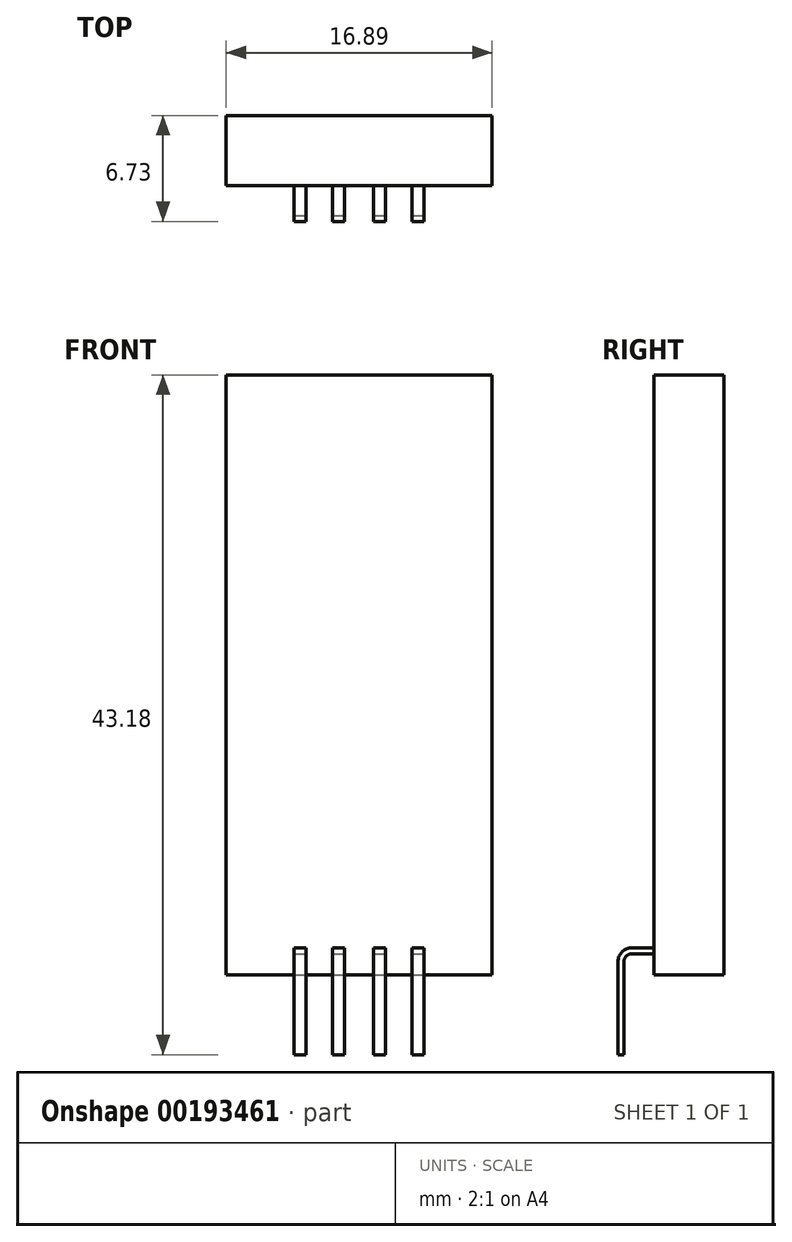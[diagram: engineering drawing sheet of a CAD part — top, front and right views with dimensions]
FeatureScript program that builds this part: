
annotation { "Feature Type Name" : "Feature", "Feature Type Description" : "" }
export const myFeature = defineFeature(function(context is Context, id is Id, definition is map)
    precondition{}
    {
        {
            var Q0;
            Q0=qCreatedBy(makeId("Front.planeOp"),FACE);
            var sketch = newSketch(context, id + "F0", { "sketchPlane" : qUnion([Q0])});
            skLineSegment(sketch, "E0.bottom", {"start": v(0, 0) * mm, "end": v(16.9, 0) * mm});
            skLineSegment(sketch, "E0.top", {"start": v(0, 38.1) * mm, "end": v(16.9, 38.1) * mm});
            skLineSegment(sketch, "E0.left", {"start": v(0, 0) * mm, "end": v(0, 38.1) * mm});
            skLineSegment(sketch, "E0.right", {"start": v(16.9, 0) * mm, "end": v(16.9, 38.1) * mm});
            skSolve(sketch);
        }
        {
            var Q0;
            Q0=makeQuery(id+"F0.imprint","IMPRINT",FACE,{"disambiguationData":[TD([[makeQuery(id+"F0.imprint","IMPRINT",EDGE,{"derivedFrom":sQuery(id+"F0.wireOp",EDGE,"E0.bottom")}),1.0]])]});
            extrude(context, id + "F1", {"entities" : qUnion([Q0]), "depth" : 4.44 * mm});
        }
        {
            var Q0;
            Q0=makeQuery(id+"F1.opExtrude","SWEPT_FACE",FACE,{"disambiguationData":[OSD([sQuery(id+"F0.wireOp",EDGE,"E0.right")])]});
            var sketch = newSketch(context, id + "F2", { "sketchPlane" : qUnion([Q0])});
            skLineSegment(sketch, "E1", {"start": v(-6.35, -5.08) * mm, "end": v(-6.35, 0.82) * mm});
            skLineSegment(sketch, "E2", {"start": v(-5.84, 1.33) * mm, "end": v(-4.45, 1.33) * mm});
            skArc(sketch, "E3.filletArc", {"start": v(-5.84, 1.33) * mm, "mid": v(-6.2, 1.18) * mm, "end": v(-6.35, 0.82) * mm});
            skLineSegment(sketch, "E4.0", {"start": v(-5.84, 1.71) * mm, "end": v(-4.45, 1.71) * mm});
            skArc(sketch, "E4.1", {"start": v(-5.84, 1.71) * mm, "mid": v(-6.47, 1.45) * mm, "end": v(-6.73, 0.82) * mm});
            skLineSegment(sketch, "E4.2", {"start": v(-6.73, -5.08) * mm, "end": v(-6.73, 0.82) * mm});
            skLineSegment(sketch, "E5", {"start": v(-6.73, -5.08) * mm, "end": v(-6.35, -5.08) * mm});
            skLineSegment(sketch, "E6", {"start": v(-4.45, 1.33) * mm, "end": v(-4.45, 1.71) * mm});
            skSolve(sketch);
        }
        {
            var Q0;
            Q0=makeQuery(id+"F2.imprint","IMPRINT",FACE,{"disambiguationData":[TD([[makeQuery(id+"F2.imprint","IMPRINT",EDGE,{"derivedFrom":sQuery(id+"F2.wireOp",EDGE,"E1")}),1.0]])]});
            var Q1;
            Q1=makeQuery(id+"F1.opExtrude","SWEPT_FACE",FACE,{"disambiguationData":[OSD([sQuery(id+"F0.wireOp",EDGE,"E0.left")])]});
            extrude(context, id + "F3", {"entities" : qUnion([Q0]), "endBound" : BoundingType.UP_TO_SURFACE, "oppositeDirection" : true, "endBoundEntityFace" : qUnion([Q1]), "depth" : 25.4 * mm});
        }
        {
            var Q0;
            Q0=makeQuery(id+"F1.opExtrude","CAP_FACE",FACE,{"disambiguationData":[OSD([sQuery(id+"F0.wireOp",EDGE,"E0.bottom"),sQuery(id+"F0.wireOp",EDGE,"E0.top"),sQuery(id+"F0.wireOp",EDGE,"E0.left"),sQuery(id+"F0.wireOp",EDGE,"E0.right")])],"isStart":false});
            var sketch = newSketch(context, id + "F4", { "sketchPlane" : qUnion([Q0])});
            skLineSegment(sketch, "E7", {"start": v(8.45, -5.17) * mm, "end": v(8.45, 2.43) * mm, "construction": true});
            skPoint(sketch, "E7.startSnap0", {"position": v(8.45, 38.1) * mm});
            skPoint(sketch, "E7.endSnap0", {"position": v(8.45, 0) * mm});
            skLineSegment(sketch, "E8", {"start": v(4.32, -6.24) * mm, "end": v(4.32, 3.07) * mm});
            skLineSegment(sketch, "E9", {"start": v(5.08, -6.3) * mm, "end": v(5.08, 3) * mm});
            skLineSegment(sketch, "E10.MirrorCS", {"start": v(11.81, -6.3) * mm, "end": v(11.81, 3) * mm});
            skLineSegment(sketch, "E11.MirrorCS", {"start": v(12.57, -6.24) * mm, "end": v(12.57, 3.07) * mm});
            skLineSegment(sketch, "E12", {"start": v(7.53, -6.3) * mm, "end": v(7.53, 3.07) * mm});
            skLineSegment(sketch, "E13.MirrorCS", {"start": v(9.36, -6.3) * mm, "end": v(9.36, 3.07) * mm});
            skLineSegment(sketch, "E14", {"start": v(6.77, -6.38) * mm, "end": v(6.77, 3.21) * mm});
            skLineSegment(sketch, "E15.MirrorCS", {"start": v(10.12, -6.38) * mm, "end": v(10.12, 3.21) * mm});
            skLineSegment(sketch, "E16", {"start": v(4.32, -6.24) * mm, "end": v(-1.02, -6.24) * mm});
            skLineSegment(sketch, "E17", {"start": v(-1.02, -6.24) * mm, "end": v(-1.02, 3.07) * mm});
            skLineSegment(sketch, "E18", {"start": v(-1.02, 3.07) * mm, "end": v(4.32, 3.07) * mm});
            skLineSegment(sketch, "E19.MirrorCS", {"start": v(17.9, 3.07) * mm, "end": v(12.57, 3.07) * mm});
            skLineSegment(sketch, "E20.MirrorCS", {"start": v(17.9, -6.24) * mm, "end": v(17.9, 3.07) * mm});
            skLineSegment(sketch, "E21.MirrorCS", {"start": v(12.57, -6.24) * mm, "end": v(17.9, -6.24) * mm});
            skLineSegment(sketch, "E22", {"start": v(5.08, 3) * mm, "end": v(6.77, 3.21) * mm});
            skLineSegment(sketch, "E23", {"start": v(5.08, -6.3) * mm, "end": v(6.77, -6.38) * mm});
            skLineSegment(sketch, "E24", {"start": v(7.53, -6.3) * mm, "end": v(9.36, -6.3) * mm});
            skLineSegment(sketch, "E25", {"start": v(7.53, 3.07) * mm, "end": v(9.36, 3.07) * mm});
            skLineSegment(sketch, "E26", {"start": v(10.12, -6.38) * mm, "end": v(11.81, -6.3) * mm});
            skLineSegment(sketch, "E27", {"start": v(10.12, 3.21) * mm, "end": v(11.81, 3) * mm});
            skSolve(sketch);
        }
        {
            var Q0;
            {var subQ1=sQuery(id+"F4.wireOp",EDGE,"E20.MirrorCS");Q0=makeQuery(id+"F4.imprint","IMPRINT",FACE,{"disambiguationData":[TD([[makeQuery(id+"F4.imprint","IMPRINT",EDGE,{"derivedFrom":subQ1}),1.0]])]});}
            var Q1;
            {var subQ0=sQuery(id+"F4.wireOp",EDGE,"E19.MirrorCS");var subQ1=sQuery(id+"F4.wireOp",EDGE,"E11.MirrorCS");var subQ2=makeQuery(id+"F4.imprint","INTERSECT",VERTEX,{"derivedFrom":[subQ1,subQ0]});Q1=makeQuery(id+"F4.imprint","IMPRINT",FACE,{"disambiguationData":[TD([[makeQuery(id+"F4.imprint","IMPRINT",EDGE,{"disambiguationData":[TD([[subQ2,1.0]])],"derivedFrom":subQ1}),-1.0]])]});}
            var Q2;
            {var subQ4=sQuery(id+"F4.wireOp",EDGE,"E16");Q2=makeQuery(id+"F4.imprint","IMPRINT",FACE,{"disambiguationData":[TD([[makeQuery(id+"F4.imprint","IMPRINT",EDGE,{"derivedFrom":subQ4}),-1.0]])]});}
            var Q3;
            {var subQ0=sQuery(id+"F4.wireOp",EDGE,"E18");var subQ1=sQuery(id+"F4.wireOp",EDGE,"E8");var subQ2=makeQuery(id+"F4.imprint","INTERSECT",VERTEX,{"derivedFrom":[subQ1,subQ0]});Q3=makeQuery(id+"F4.imprint","IMPRINT",FACE,{"disambiguationData":[TD([[makeQuery(id+"F4.imprint","IMPRINT",EDGE,{"disambiguationData":[TD([[subQ2,1.0]])],"derivedFrom":subQ1}),1.0]])]});}
            var Q4;
            {var subQ0=sQuery(id+"F4.wireOp",EDGE,"E23");Q4=makeQuery(id+"F4.imprint","IMPRINT",FACE,{"disambiguationData":[TD([[makeQuery(id+"F4.imprint","IMPRINT",EDGE,{"derivedFrom":subQ0}),1.0]])]});}
            var Q5;
            {var subQ0=sQuery(id+"F4.wireOp",EDGE,"E22");Q5=makeQuery(id+"F4.imprint","IMPRINT",FACE,{"disambiguationData":[TD([[makeQuery(id+"F4.imprint","IMPRINT",EDGE,{"derivedFrom":subQ0}),-1.0]])]});}
            var Q6;
            {var subQ0=sQuery(id+"F4.wireOp",EDGE,"E25");Q6=makeQuery(id+"F4.imprint","IMPRINT",FACE,{"disambiguationData":[TD([[makeQuery(id+"F4.imprint","IMPRINT",EDGE,{"derivedFrom":subQ0}),-1.0]])]});}
            var Q7;
            {var subQ0=sQuery(id+"F4.wireOp",EDGE,"E27");Q7=makeQuery(id+"F4.imprint","IMPRINT",FACE,{"disambiguationData":[TD([[makeQuery(id+"F4.imprint","IMPRINT",EDGE,{"derivedFrom":subQ0}),-1.0]])]});}
            var Q8;
            {var subQ0=sQuery(id+"F4.wireOp",EDGE,"E26");Q8=makeQuery(id+"F4.imprint","IMPRINT",FACE,{"disambiguationData":[TD([[makeQuery(id+"F4.imprint","IMPRINT",EDGE,{"derivedFrom":subQ0}),1.0]])]});}
            var Q9;
            {var subQ0=sQuery(id+"F4.wireOp",EDGE,"E24");Q9=makeQuery(id+"F4.imprint","IMPRINT",FACE,{"disambiguationData":[TD([[makeQuery(id+"F4.imprint","IMPRINT",EDGE,{"derivedFrom":subQ0}),1.0]])]});}
            extrude(context, id + "F5", {"entities" : qUnion([Q0, Q1, Q2, Q3, Q4, Q5, Q6, Q7, Q8, Q9]), "operationType" : NewBodyOperationType.REMOVE, "depth" : 25.4 * mm});
        }
    });
